# Revit family: BLE-G-WHS-G4-LED
name_source: partatom
category: Lighting Fixtures
units: mm (PartAtom-declared; Revit-internal decimal feet)

## family parameters
Cut with Voids When Loaded = No
Host = Face
Light Source = Yes
Maintain Annotation Orientation = No
Part Type = Normal
Room Calculation Point = No
Round Connector Dimension = Use Diameter
Shared = No

## types (14) — shared parameters
Base Material = 100 - Black
Color Filter = 16777215
Default Elevation = 4' - 0"
Dimming Lamp Color Temperature Shift = <None>
Gooseneck Material = 100 - Black
Photometric Web File = generic
Shade Material = 100 - Black
Tilt Angle = 0.00°

## per-type parameters (varying)
| type | 12" | 14" | 16" | 18" | 20" | 24" | 28" | Dome | Flat | Heat Sink |
| 12" Dome | Yes | No | No | No | No | No | No | Yes | No | 0' - 7 3/32" |
| 14" Dome | No | Yes | No | No | No | No | No | Yes | No | 0' - 6 29/32" |
| 16" Dome | No | No | Yes | No | No | No | No | Yes | No | 0' - 6 29/32" |
| 18" Dome | No | No | No | Yes | No | No | No | Yes | No | 0' - 6 29/32" |
| 20" Dome | No | No | No | No | Yes | No | No | Yes | No | 0' - 6 29/32" |
| 24" Dome | No | No | No | No | No | Yes | No | Yes | No | 0' - 7 3/32" |
| 28" Dome | No | No | No | No | No | No | Yes | Yes | No | 0' - 6 29/32" |
| 12" Flat | Yes | No | No | No | No | No | No | No | Yes | 0' - 7 3/32" |
| 14" Flat | No | Yes | No | No | No | No | No | No | Yes | 0' - 6 29/32" |
| 16" Flat | No | No | Yes | No | No | No | No | No | Yes | 0' - 6 29/32" |
| 18" Flat | No | No | No | Yes | No | No | No | No | Yes | 0' - 6 29/32" |
| 20" Flat | No | No | No | No | Yes | No | No | No | Yes | 0' - 6 29/32" |
| 24" Flat | No | No | No | No | No | Yes | No | No | Yes | 0' - 7 3/32" |
| 28" Flat | No | No | No | No | No | No | Yes | No | Yes | 0' - 6 29/32" |

## geometry (parser evidence)
native form markers: Sweep x46
no freeform markers — native parametric forms only
